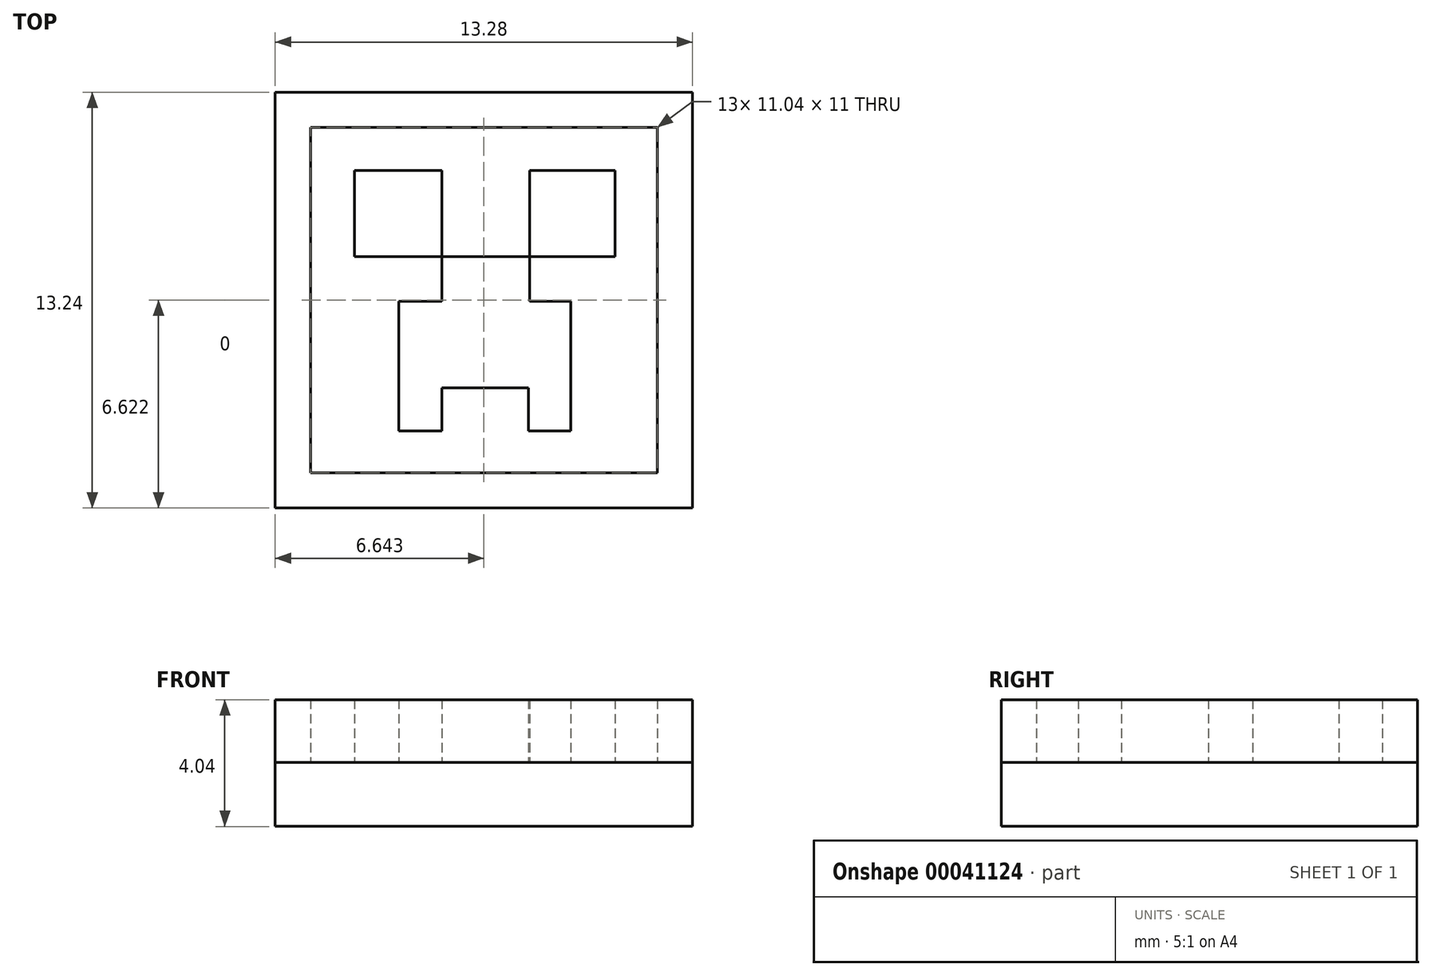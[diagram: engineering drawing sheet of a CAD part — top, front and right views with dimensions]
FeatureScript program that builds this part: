
annotation { "Feature Type Name" : "Feature", "Feature Type Description" : "" }
export const myFeature = defineFeature(function(context is Context, id is Id, definition is map)
    precondition{}
    {
        {
            var Q0;
            Q0=qCreatedBy(makeId("Top.planeOp"),FACE);
            var sketch = newSketch(context, id + "F0", { "sketchPlane" : qUnion([Q0])});
            skLineSegment(sketch, "E0.bottom", {"start": v(1.2, 12.68) * mm, "end": v(12.24, 12.68) * mm});
            skLineSegment(sketch, "E0.top", {"start": v(1.2, 1.68) * mm, "end": v(12.24, 1.68) * mm});
            skLineSegment(sketch, "E0.left", {"start": v(1.2, 12.68) * mm, "end": v(1.2, 1.68) * mm});
            skLineSegment(sketch, "E0.right", {"start": v(12.24, 12.68) * mm, "end": v(12.24, 1.68) * mm});
            skLineSegment(sketch, "E1.0", {"start": v(0.08, 13.8) * mm, "end": v(0.08, 0.56) * mm});
            skLineSegment(sketch, "E1.1", {"start": v(0.08, 13.8) * mm, "end": v(13.36, 13.8) * mm});
            skLineSegment(sketch, "E1.2", {"start": v(13.36, 13.8) * mm, "end": v(13.36, 0.56) * mm});
            skLineSegment(sketch, "E1.3", {"start": v(0.08, 0.56) * mm, "end": v(13.36, 0.56) * mm});
            skLineSegment(sketch, "E2.bottom", {"start": v(2.6, 11.3) * mm, "end": v(5.4, 11.3) * mm});
            skLineSegment(sketch, "E2.top", {"start": v(2.6, 8.56) * mm, "end": v(5.4, 8.56) * mm});
            skLineSegment(sketch, "E2.left", {"start": v(2.6, 11.3) * mm, "end": v(2.6, 8.56) * mm});
            skLineSegment(sketch, "E2.right", {"start": v(5.4, 11.3) * mm, "end": v(5.4, 8.56) * mm});
            skLineSegment(sketch, "E3", {"start": v(8.18, 11.3) * mm, "end": v(10.9, 11.3) * mm});
            skLineSegment(sketch, "E4", {"start": v(10.9, 11.3) * mm, "end": v(10.9, 8.56) * mm});
            skLineSegment(sketch, "E5", {"start": v(10.9, 8.56) * mm, "end": v(8.18, 8.56) * mm});
            skLineSegment(sketch, "E6", {"start": v(8.18, 8.56) * mm, "end": v(8.18, 11.3) * mm});
            skLineSegment(sketch, "E7", {"start": v(5.4, 8.56) * mm, "end": v(8.18, 8.56) * mm});
            skLineSegment(sketch, "E8", {"start": v(8.18, 8.56) * mm, "end": v(8.18, 7.15) * mm});
            skLineSegment(sketch, "E9", {"start": v(8.18, 7.15) * mm, "end": v(9.48, 7.15) * mm});
            skLineSegment(sketch, "E10", {"start": v(9.48, 7.15) * mm, "end": v(9.48, 3) * mm});
            skLineSegment(sketch, "E11", {"start": v(9.48, 3) * mm, "end": v(8.13, 3) * mm});
            skLineSegment(sketch, "E12", {"start": v(8.13, 3) * mm, "end": v(8.13, 4.38) * mm});
            skLineSegment(sketch, "E13", {"start": v(8.13, 4.38) * mm, "end": v(5.4, 4.38) * mm});
            skLineSegment(sketch, "E14", {"start": v(5.4, 4.38) * mm, "end": v(5.4, 3) * mm});
            skLineSegment(sketch, "E15", {"start": v(5.4, 3) * mm, "end": v(4.02, 3) * mm});
            skLineSegment(sketch, "E16", {"start": v(4.02, 3) * mm, "end": v(4.02, 7.15) * mm});
            skLineSegment(sketch, "E17", {"start": v(4.02, 7.15) * mm, "end": v(5.4, 7.15) * mm});
            skLineSegment(sketch, "E18", {"start": v(5.4, 7.15) * mm, "end": v(5.4, 8.56) * mm});
            skSolve(sketch);
        }
        {
            var Q0;
            Q0 = qSketchRegion(id + "F0", true);
            var Q1;
            Q1=makeQuery(id+"F0.imprint","IMPRINT",FACE,{"disambiguationData":[TD([[makeQuery(id+"F0.imprint","IMPRINT",EDGE,{"derivedFrom":sQuery(id+"F0.wireOp",EDGE,"E7")}),-1.0]])]});
            var Q2;
            Q2=makeQuery(id+"F0.imprint","IMPRINT",FACE,{"disambiguationData":[TD([[makeQuery(id+"F0.imprint","IMPRINT",EDGE,{"derivedFrom":sQuery(id+"F0.wireOp",EDGE,"E2.bottom")}),-1.0]])]});
            var Q3;
            Q3=makeQuery(id+"F0.imprint","IMPRINT",FACE,{"disambiguationData":[TD([[makeQuery(id+"F0.imprint","IMPRINT",EDGE,{"derivedFrom":sQuery(id+"F0.wireOp",EDGE,"E3")}),-1.0]])]});
            extrude(context, id + "F1", {"entities" : qUnion([Q0, Q1, Q2, Q3]), "depth" : 2 * mm});
        }
        {
            var Q0;
            Q0=makeQuery(id+"F1.opExtrude","SWEPT_FACE",FACE,{"disambiguationData":[OSD([sQuery(id+"F0.wireOp",EDGE,"E1.0")])]});
            var sketch = newSketch(context, id + "F2", { "sketchPlane" : qUnion([Q0])});
            skLineSegment(sketch, "E19", {"start": v(-13.8, 0) * mm, "end": v(-13.8, -2.04) * mm});
            skLineSegment(sketch, "E20", {"start": v(-13.8, -2.04) * mm, "end": v(-0.56, -2.04) * mm});
            skLineSegment(sketch, "E21", {"start": v(-0.56, -2.04) * mm, "end": v(-0.56, 0) * mm});
            skSolve(sketch);
        }
        {
            var Q0;
            Q0 = qSketchRegion(id + "F2", true);
            var Q1;
            Q1=makeQuery(id+"F2.imprint","IMPRINT",FACE,{"disambiguationData":[TD([[makeQuery(id+"F2.imprint","IMPRINT",EDGE,{"derivedFrom":sQuery(id+"F2.wireOp",EDGE,"E19")}),1.0]])]});
            var Q2;
            Q2=makeQuery(id+"F1.opExtrude","SWEPT_FACE",FACE,{"disambiguationData":[OSD([sQuery(id+"F0.wireOp",EDGE,"E1.2")])]});
            extrude(context, id + "F3", {"entities" : qUnion([Q0, Q1]), "endBound" : BoundingType.UP_TO_SURFACE, "oppositeDirection" : true, "endBoundEntityFace" : qUnion([Q2]), "depth" : 25 * mm});
        }
    });
